# Revit family: fire rated valve BIM
name_source: partatom
category: Specialty Equipment
units: mm (PartAtom-declared; Revit-internal decimal feet)

## family parameters
Always vertical = Yes
Cut with Voids When Loaded = No
Enable Cutting in Views = No
Host = Ceiling
Maintain Annotation Orientation = No
Part Type = Normal
Room Calculation Point = No
Round Connector Dimension = Use Diameter
Shared = No

## types (2) — shared parameters
Cut_Out_Rad = 74 mm
Disc_Rad = 57 mm  [stored 0.187008 ft]
Holder_Depth = 36 mm
IFC Classification = Building Element Proxy
InsideRadius = 60 mm
Manufacturer = Airflow Developments
Material = Intumescent Sealant
OutsideRadius = 62 mm
Overall_Rad = 85 mm  [stored 0.278871 ft]
Performance = BS EN 1366-3:2009 & BS 476, ETA-12/0332, 1224-CPR-0341, CE Marked
Valve_Rad = 67 mm
zero-valued in all types: Default Elevation

## per-type parameters (varying)
| type | Description | Extract_Valve | Part numbers | Supply_Valve |
| Supply - 125mm | Ø125mm Fire Rated Supply Valve | No | 90002218, 90002219 | Yes |
| Extract - 125mm | Ø125mm Fire Rated Extract Valve | Yes | 90002216, 90002217 | No |

note: [stored X ft] marks values corroborated as IEEE doubles in the binary element streams (Revit-internal decimal feet)

## geometry (parser evidence)
native form markers: Blend x2, Sweep x3
no freeform markers — native parametric forms only
